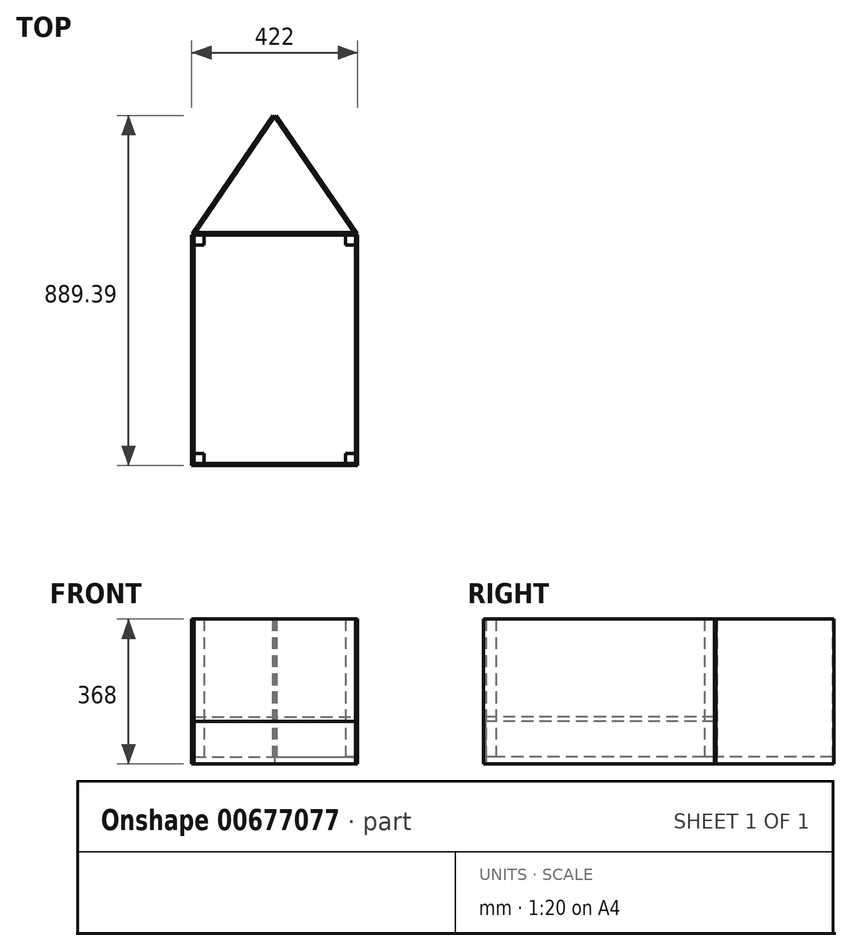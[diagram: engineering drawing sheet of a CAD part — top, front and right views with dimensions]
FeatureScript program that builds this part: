
annotation { "Feature Type Name" : "Feature", "Feature Type Description" : "" }
export const myFeature = defineFeature(function(context is Context, id is Id, definition is map)
    precondition{}
    {
        {
            var Q0;
            Q0=qCreatedBy(makeId("Top.planeOp"),FACE);
            var sketch = newSketch(context, id + "F0", { "sketchPlane" : qUnion([Q0])});
            skLineSegment(sketch, "E0.bottom", {"start": v(-205, 290) * mm, "end": v(205, 290) * mm});
            skLineSegment(sketch, "E0.top", {"start": v(-205, -290) * mm, "end": v(205, -290) * mm});
            skLineSegment(sketch, "E0.left", {"start": v(-205, 290) * mm, "end": v(-205, -290) * mm});
            skLineSegment(sketch, "E0.right", {"start": v(205, 290) * mm, "end": v(205, -290) * mm});
            skLineSegment(sketch, "E1", {"start": v(0, 290) * mm, "end": v(0, -290) * mm, "construction": true});
            skLineSegment(sketch, "E2", {"start": v(-205, 0) * mm, "end": v(205, 0) * mm, "construction": true});
            skSolve(sketch);
        }
        {
            var Q0;
            Q0 = qSketchRegion(id + "F0", true);
            extrude(context, id + "F1", {"entities" : qUnion([Q0]), "depth" : 18 * mm, "offsetDistance" : 25 * mm});
        }
        {
            var Q0;
            Q0=makeQuery(id+"F1.opExtrude","CAP_FACE",FACE,{"disambiguationData":[OSD([sQuery(id+"F0.wireOp",EDGE,"E0.bottom"),sQuery(id+"F0.wireOp",EDGE,"E0.top"),sQuery(id+"F0.wireOp",EDGE,"E0.left"),sQuery(id+"F0.wireOp",EDGE,"E0.right")])],"isStart":false});
            var sketch = newSketch(context, id + "F2", { "sketchPlane" : qUnion([Q0])});
            skLineSegment(sketch, "E3.bottom", {"start": v(-205, -290) * mm, "end": v(-179.6, -290) * mm});
            skLineSegment(sketch, "E3.top", {"start": v(-205, -264.6) * mm, "end": v(-179.6, -264.6) * mm});
            skLineSegment(sketch, "E3.left", {"start": v(-205, -290) * mm, "end": v(-205, -264.6) * mm});
            skLineSegment(sketch, "E3.right", {"start": v(-179.6, -290) * mm, "end": v(-179.6, -264.6) * mm});
            skSolve(sketch);
        }
        {
            var Q0;
            Q0=makeQuery(id+"F2.imprint","IMPRINT",FACE,{"disambiguationData":[TD([[makeQuery(id+"F2.imprint","IMPRINT",EDGE,{"derivedFrom":sQuery(id+"F2.wireOp",EDGE,"E3.bottom")}),1.0]])]});
            extrude(context, id + "F3", {"entities" : qUnion([Q0]), "depth" : 350 * mm, "offsetDistance" : 25 * mm});
        }
        {
            var Q0;
            Q0=makeQuery(id+"F3.opExtrude","SWEPT_BODY",BODY,{"disambiguationData":[OSD([sQuery(id+"F2.wireOp",EDGE,"E3.bottom"),sQuery(id+"F2.wireOp",EDGE,"E3.top"),sQuery(id+"F2.wireOp",EDGE,"E3.left"),sQuery(id+"F2.wireOp",EDGE,"E3.right")])]});
            var Q1;
            Q1=qCreatedBy(makeId("Front.planeOp"),FACE);
            mirror(context, id + "F4", {"entities" : qUnion([Q0]), "mirrorPlane" : qUnion([Q1])});
        }
        {
            var Q0;
            Q0=makeQuery(id+"F4.opPattern","COPY",BODY,{"derivedFrom":makeQuery(id+"F3.opExtrude","SWEPT_BODY",BODY,{"disambiguationData":[OSD([sQuery(id+"F2.wireOp",EDGE,"E3.bottom"),sQuery(id+"F2.wireOp",EDGE,"E3.top"),sQuery(id+"F2.wireOp",EDGE,"E3.left"),sQuery(id+"F2.wireOp",EDGE,"E3.right")])]}),"instanceName":"1"});
            var Q1;
            Q1=makeQuery(id+"F3.opExtrude","SWEPT_BODY",BODY,{"disambiguationData":[OSD([sQuery(id+"F2.wireOp",EDGE,"E3.bottom"),sQuery(id+"F2.wireOp",EDGE,"E3.top"),sQuery(id+"F2.wireOp",EDGE,"E3.left"),sQuery(id+"F2.wireOp",EDGE,"E3.right")])]});
            var Q2;
            Q2=qCreatedBy(makeId("Right.planeOp"),FACE);
            mirror(context, id + "F5", {"entities" : qUnion([Q0, Q1]), "mirrorPlane" : qUnion([Q2])});
        }
        {
            var Q0;
            Q0=makeQuery(id+"F1.opExtrude","CAP_FACE",FACE,{"disambiguationData":[OSD([sQuery(id+"F0.wireOp",EDGE,"E0.bottom"),sQuery(id+"F0.wireOp",EDGE,"E0.top"),sQuery(id+"F0.wireOp",EDGE,"E0.left"),sQuery(id+"F0.wireOp",EDGE,"E0.right")])],"isStart":false});
            cPlane(context, id + "F6", {"entities" : qUnion([Q0]), "cplaneType" : CPlaneType.OFFSET, "offset" : 90 * mm, "width" : 150 * mm, "height" : 150 * mm});
        }
        {
            var Q0;
            Q0=qCreatedBy(id+"F6.planeOp",FACE);
            var sketch = newSketch(context, id + "F7", { "sketchPlane" : qUnion([Q0])});
            skLineSegment(sketch, "E4.bottom", {"start": v(-205, 290) * mm, "end": v(205, 290) * mm});
            skLineSegment(sketch, "E4.top", {"start": v(-205, -290) * mm, "end": v(205, -290) * mm});
            skLineSegment(sketch, "E4.left", {"start": v(-205, 290) * mm, "end": v(-205, -290) * mm});
            skLineSegment(sketch, "E4.right", {"start": v(205, 290) * mm, "end": v(205, -290) * mm});
            skSolve(sketch);
        }
        {
            var Q0;
            Q0 = qSketchRegion(id + "F7", true);
            extrude(context, id + "F8", {"entities" : qUnion([Q0]), "depth" : 12 * mm, "offsetDistance" : 25 * mm});
        }
        {
            var Q0;
            Q0=qCreatedBy(makeId("Top.planeOp"),FACE);
            var sketch = newSketch(context, id + "F9", { "sketchPlane" : qUnion([Q0])});
            skLineSegment(sketch, "E5", {"start": v(0, 590) * mm, "end": v(205, 290) * mm});
            skLineSegment(sketch, "E6", {"start": v(205, 290) * mm, "end": v(-205, 290) * mm});
            skLineSegment(sketch, "E7", {"start": v(-205, 290) * mm, "end": v(0, 590) * mm});
            skSolve(sketch);
        }
        {
            var Q0;
            Q0=makeQuery(id+"F9.imprint","IMPRINT",FACE,{"disambiguationData":[TD([[makeQuery(id+"F9.imprint","IMPRINT",EDGE,{"derivedFrom":sQuery(id+"F9.wireOp",EDGE,"E5")}),-1.0]])]});
            extrude(context, id + "F10", {"entities" : qUnion([Q0]), "operationType" : NewBodyOperationType.ADD, "depth" : 18 * mm, "offsetDistance" : 25 * mm});
        }
        {
            var Q0;
            Q0=makeQuery(id+"F5.opPattern","COPY",FACE,{"derivedFrom":makeQuery(id+"F3.opExtrude","SWEPT_FACE",FACE,{"disambiguationData":[OSD([sQuery(id+"F2.wireOp",EDGE,"E3.bottom")])]}),"instanceName":"1"});
            var sketch = newSketch(context, id + "F11", { "sketchPlane" : qUnion([Q0])});
            skLineSegment(sketch, "E8.bottom", {"start": v(-205, 0) * mm, "end": v(205, 0) * mm});
            skLineSegment(sketch, "E8.top", {"start": v(-205, 108) * mm, "end": v(205, 108) * mm});
            skLineSegment(sketch, "E8.left", {"start": v(-205, 0) * mm, "end": v(-205, 108) * mm});
            skLineSegment(sketch, "E8.right", {"start": v(205, 0) * mm, "end": v(205, 108) * mm});
            skSolve(sketch);
        }
        {
            var Q0;
            Q0 = qSketchRegion(id + "F11", true);
            extrude(context, id + "F12", {"entities" : qUnion([Q0]), "depth" : 6 * mm, "offsetDistance" : 25 * mm});
        }
        {
            var Q0;
            Q0=makeQuery(id+"F5.opPattern","COPY",FACE,{"derivedFrom":makeQuery(id+"F3.opExtrude","SWEPT_FACE",FACE,{"disambiguationData":[OSD([sQuery(id+"F2.wireOp",EDGE,"E3.bottom")])]}),"instanceName":"1"});
            var sketch = newSketch(context, id + "F13", { "sketchPlane" : qUnion([Q0])});
            skLineSegment(sketch, "E9.bottom", {"start": v(-205, 368) * mm, "end": v(205, 368) * mm});
            skLineSegment(sketch, "E9.top", {"start": v(-205, 108) * mm, "end": v(205, 108) * mm});
            skLineSegment(sketch, "E9.left", {"start": v(-205, 368) * mm, "end": v(-205, 108) * mm});
            skLineSegment(sketch, "E9.right", {"start": v(205, 368) * mm, "end": v(205, 108) * mm});
            skSolve(sketch);
        }
        {
            var Q0;
            Q0 = qSketchRegion(id + "F13", true);
            extrude(context, id + "F14", {"entities" : qUnion([Q0]), "depth" : 6 * mm, "offsetDistance" : 25 * mm});
        }
        {
            var Q0;
            Q0=makeQuery(id+"F10.boolean.opBoolean","MERGE",FACE,{"derivedFrom":[makeQuery(id+"F1.opExtrude","SWEPT_FACE",FACE,{"disambiguationData":[OSD([sQuery(id+"F0.wireOp",EDGE,"E0.left")])]}),makeQuery(id+"F4.opPattern","COPY",FACE,{"derivedFrom":makeQuery(id+"F3.opExtrude","SWEPT_FACE",FACE,{"disambiguationData":[OSD([sQuery(id+"F2.wireOp",EDGE,"E3.left")])]}),"instanceName":"1"})]});
            var sketch = newSketch(context, id + "F15", { "sketchPlane" : qUnion([Q0])});
            skLineSegment(sketch, "E10.bottom", {"start": v(-290, 368) * mm, "end": v(296, 368) * mm});
            skLineSegment(sketch, "E10.top", {"start": v(-290, 0) * mm, "end": v(296, 0) * mm});
            skLineSegment(sketch, "E10.left", {"start": v(-290, 368) * mm, "end": v(-290, 0) * mm});
            skLineSegment(sketch, "E10.right", {"start": v(296, 368) * mm, "end": v(296, 0) * mm});
            skSolve(sketch);
        }
        {
            var Q0;
            Q0 = qSketchRegion(id + "F15", true);
            extrude(context, id + "F16", {"entities" : qUnion([Q0]), "depth" : 6 * mm, "offsetDistance" : 25 * mm});
        }
        {
            var Q0;
            Q0=makeQuery(id+"F16.opExtrude","SWEPT_BODY",BODY,{"disambiguationData":[OSD([sQuery(id+"F15.wireOp",EDGE,"E10.bottom"),sQuery(id+"F15.wireOp",EDGE,"E10.top"),sQuery(id+"F15.wireOp",EDGE,"E10.left"),sQuery(id+"F15.wireOp",EDGE,"E10.right")])]});
            var Q1;
            Q1=qCreatedBy(makeId("Right.planeOp"),FACE);
            mirror(context, id + "F17", {"entities" : qUnion([Q0]), "mirrorPlane" : qUnion([Q1])});
        }
        {
            var Q0;
            Q0=makeQuery(id+"F10.opExtrude","SWEPT_FACE",FACE,{"disambiguationData":[OSD([sQuery(id+"F9.wireOp",EDGE,"E5")])]});
            var sketch = newSketch(context, id + "F18", { "sketchPlane" : qUnion([Q0])});
            skLineSegment(sketch, "E11.bottom", {"start": v(123.78, 368) * mm, "end": v(487.13, 368) * mm});
            skLineSegment(sketch, "E11.top", {"start": v(123.78, 0) * mm, "end": v(487.13, 0) * mm});
            skLineSegment(sketch, "E11.left", {"start": v(123.78, 368) * mm, "end": v(123.78, 0) * mm});
            skLineSegment(sketch, "E11.right", {"start": v(487.13, 368) * mm, "end": v(487.13, 0) * mm});
            skSolve(sketch);
        }
        {
            var Q0;
            Q0 = qSketchRegion(id + "F18", true);
            extrude(context, id + "F19", {"entities" : qUnion([Q0]), "depth" : 6 * mm, "offsetDistance" : 25 * mm});
        }
        {
            var Q0;
            Q0=makeQuery(id+"F19.opExtrude","SWEPT_BODY",BODY,{"disambiguationData":[OSD([sQuery(id+"F18.wireOp",EDGE,"E11.bottom"),sQuery(id+"F18.wireOp",EDGE,"E11.top"),sQuery(id+"F18.wireOp",EDGE,"E11.left"),sQuery(id+"F18.wireOp",EDGE,"E11.right")])]});
            var Q1;
            Q1=qCreatedBy(makeId("Right.planeOp"),FACE);
            mirror(context, id + "F20", {"entities" : qUnion([Q0]), "mirrorPlane" : qUnion([Q1])});
        }
        {
            var Q0;
            Q0=makeQuery(id+"F10.boolean.opBoolean","MERGE",FACE,{"derivedFrom":[makeQuery(id+"F1.opExtrude","CAP_FACE",FACE,{"disambiguationData":[OSD([sQuery(id+"F0.wireOp",EDGE,"E0.bottom"),sQuery(id+"F0.wireOp",EDGE,"E0.top"),sQuery(id+"F0.wireOp",EDGE,"E0.left"),sQuery(id+"F0.wireOp",EDGE,"E0.right")])],"isStart":false}),makeQuery(id+"F10.opExtrude","CAP_FACE",FACE,{"disambiguationData":[OSD([sQuery(id+"F9.wireOp",EDGE,"E5"),sQuery(id+"F9.wireOp",EDGE,"E6"),sQuery(id+"F9.wireOp",EDGE,"E7")])],"isStart":false})]});
            var sketch = newSketch(context, id + "F21", { "sketchPlane" : qUnion([Q0])});
            skLineSegment(sketch, "E12.bottom", {"start": v(-205, 290) * mm, "end": v(205, 290) * mm});
            skLineSegment(sketch, "E12.top", {"start": v(-205, 296) * mm, "end": v(205, 296) * mm});
            skLineSegment(sketch, "E12.left", {"start": v(-205, 290) * mm, "end": v(-205, 296) * mm});
            skLineSegment(sketch, "E12.right", {"start": v(205, 290) * mm, "end": v(205, 296) * mm});
            skSolve(sketch);
        }
        {
            var Q0;
            Q0 = qSketchRegion(id + "F21", true);
            extrude(context, id + "F22", {"entities" : qUnion([Q0]), "depth" : 350 * mm, "offsetDistance" : 25 * mm});
        }
    });
